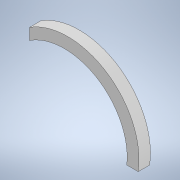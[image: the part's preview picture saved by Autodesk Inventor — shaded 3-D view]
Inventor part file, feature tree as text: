
AUTODESK INVENTOR PART (.ipt)
format: ipt  version: 2020 (Build 240168000, 168)  size: 101,376 bytes
history: native  units: in
note: dims shown in document units (in); Inventor stores cm internally (conversion verified against a paired STEP export)
features: extrude x1, sketch x1
ambient origin geometry x8: Origin, YZ Plane, XZ Plane, XY Plane, X Axis, Y Axis, Z Axis, Center Point
bodies: Solid1 (feature_tree)
feature tree (2):
  extrude  "Extrusion1"  Depth=0.5906in
  sketch  "Sketch1"  dims[d0=0.5906in d2=0.5906in d3=0.5906in d4=0.0in]
